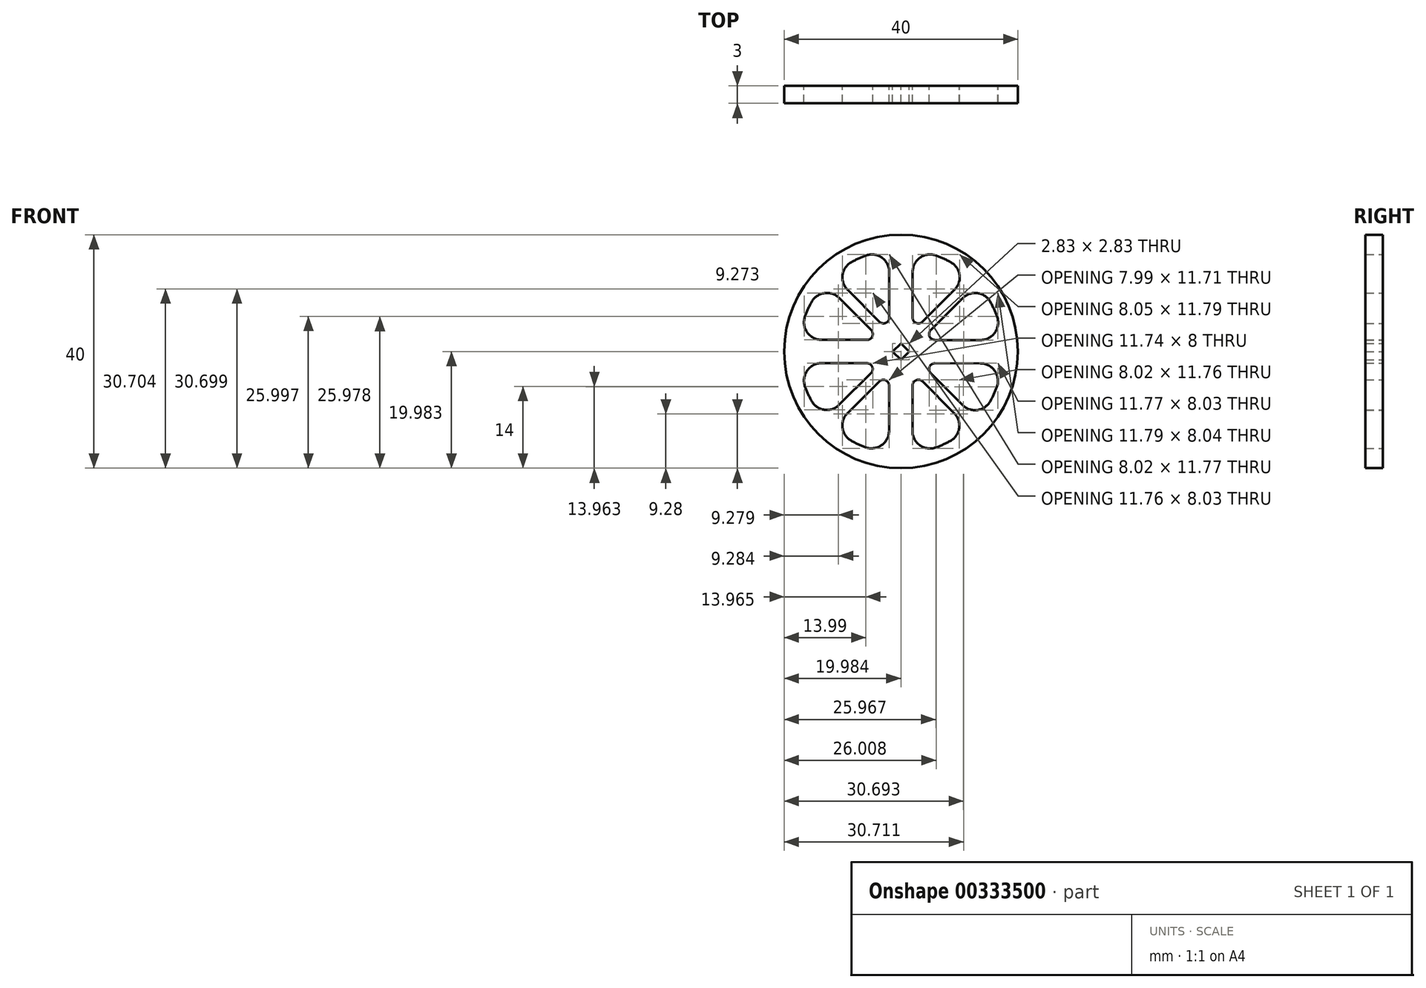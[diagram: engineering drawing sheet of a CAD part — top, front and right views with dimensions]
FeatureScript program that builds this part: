
annotation { "Feature Type Name" : "Feature", "Feature Type Description" : "" }
export const myFeature = defineFeature(function(context is Context, id is Id, definition is map)
    precondition{}
    {
        {
            var Q0;
            Q0=qCreatedBy(makeId("Front.planeOp"),FACE);
            var sketch = newSketch(context, id + "F0", { "sketchPlane" : qUnion([Q0])});
            skCircle(sketch, "E0", {"center": v(0, 0) * mm, "radius": 20 * mm});
            skArc(sketch, "E1", {"start": v(-16.43, -6.03) * mm, "mid": v(-15.92, -7.27) * mm, "end": v(-15.32, -8.46) * mm});
            skPoint(sketch, "E2", {"position": v(-2, 17.39) * mm});
            skPoint(sketch, "E3", {"position": v(2, 17.39) * mm});
            skPoint(sketch, "E4", {"position": v(-17.39, 2) * mm});
            skPoint(sketch, "E5", {"position": v(-17.39, -2) * mm});
            skPoint(sketch, "E6", {"position": v(-2.04, -17.38) * mm});
            skPoint(sketch, "E7", {"position": v(1.95, -17.4) * mm});
            skPoint(sketch, "E8", {"position": v(17.4, 1.95) * mm});
            skPoint(sketch, "E9", {"position": v(17.38, -2.05) * mm});
            skLineSegment(sketch, "E10", {"start": v(2, 13.62) * mm, "end": v(1.98, 5.8) * mm});
            skLineSegment(sketch, "E11", {"start": v(13.62, 1.96) * mm, "end": v(5.8, 1.97) * mm});
            skPoint(sketch, "E12.orphan", {"position": v(-17.5, 0) * mm});
            skLineSegment(sketch, "E13.trimOffspring", {"start": v(-2, 5.81) * mm, "end": v(-2, 13.6) * mm});
            skLineSegment(sketch, "E14.trimOffspring", {"start": v(1.97, -5.84) * mm, "end": v(1.96, -13.62) * mm});
            skLineSegment(sketch, "E15.trimOffspring", {"start": v(5.8, -2.02) * mm, "end": v(13.6, -2.04) * mm});
            skPoint(sketch, "E16.orphan", {"position": v(-0.04, -17.5) * mm});
            skArc(sketch, "E17.trimOffspring", {"start": v(5.98, -16.45) * mm, "mid": v(7.23, -15.94) * mm, "end": v(8.43, -15.33) * mm});
            skArc(sketch, "E18.trimOffspring", {"start": v(16.45, 5.98) * mm, "mid": v(15.93, 7.24) * mm, "end": v(15.32, 8.46) * mm});
            skPoint(sketch, "E19.orphan", {"position": v(17.5, -0.05) * mm});
            skLineSegment(sketch, "E20.trimOffspring", {"start": v(-5.84, 1.98) * mm, "end": v(-13.62, 2) * mm});
            skArc(sketch, "E21.trimOffspring", {"start": v(-6.04, 16.43) * mm, "mid": v(-7.28, 15.91) * mm, "end": v(-8.49, 15.3) * mm});
            skPoint(sketch, "E22.orphan", {"position": v(0, 17.5) * mm});
            skLineSegment(sketch, "E23", {"start": v(-13.6, -2) * mm, "end": v(-5.84, -2) * mm});
            skLineSegment(sketch, "E24", {"start": v(-2.04, -13.6) * mm, "end": v(-2.04, -5.86) * mm});
            skPoint(sketch, "E25", {"position": v(-13.06, 11.65) * mm});
            skPoint(sketch, "E26", {"position": v(-11.65, 13.06) * mm});
            skPoint(sketch, "E27", {"position": v(11.67, 13.05) * mm});
            skPoint(sketch, "E28", {"position": v(13.08, 11.63) * mm});
            skPoint(sketch, "E29", {"position": v(13.03, -11.68) * mm});
            skPoint(sketch, "E30", {"position": v(11.61, -13.1) * mm});
            skPoint(sketch, "E31", {"position": v(-11.66, -13.05) * mm});
            skPoint(sketch, "E32", {"position": v(-13.08, -11.63) * mm});
            skLineSegment(sketch, "E33", {"start": v(-10.56, 9.14) * mm, "end": v(-5.13, 3.7) * mm});
            skLineSegment(sketch, "E34", {"start": v(10.54, -9.18) * mm, "end": v(5.1, -3.73) * mm});
            skLineSegment(sketch, "E35", {"start": v(9.16, 10.55) * mm, "end": v(3.7, 5.1) * mm});
            skLineSegment(sketch, "E36", {"start": v(-9.16, -10.55) * mm, "end": v(-3.75, -5.15) * mm});
            skPoint(sketch, "E37.end.orphan", {"position": v(-12.37, 12.37) * mm});
            skLineSegment(sketch, "E38.trimOffspring", {"start": v(-3.71, 5.1) * mm, "end": v(-9.16, 10.56) * mm});
            skLineSegment(sketch, "E39.trimOffspring", {"start": v(-0.01, 1.4) * mm, "end": v(-1.43, -0.02) * mm});
            skLineSegment(sketch, "E40.trimOffspring", {"start": v(5.1, 3.68) * mm, "end": v(10.57, 9.13) * mm});
            skLineSegment(sketch, "E41.trimOffspring", {"start": v(1.4, -0.02) * mm, "end": v(-0.01, 1.4) * mm});
            skLineSegment(sketch, "E42.trimOffspring", {"start": v(3.68, -5.14) * mm, "end": v(9.11, -10.59) * mm});
            skPoint(sketch, "E43.end.orphan", {"position": v(12.34, -12.4) * mm});
            skLineSegment(sketch, "E44.trimOffspring", {"start": v(-5.14, -3.71) * mm, "end": v(-10.57, -9.14) * mm});
            skLineSegment(sketch, "E45.trimOffspring", {"start": v(-0.02, -1.43) * mm, "end": v(1.4, -0.02) * mm});
            skPoint(sketch, "E46.end.orphan", {"position": v(-12.39, -12.36) * mm});
            skPoint(sketch, "E47.end.orphan", {"position": v(12.4, 12.36) * mm});
            skLineSegment(sketch, "E48.trimOffspring", {"start": v(-1.43, -0.02) * mm, "end": v(-0.02, -1.43) * mm});
            skArc(sketch, "E49.trimOffspring", {"start": v(8.5, 15.3) * mm, "mid": v(7.29, 15.91) * mm, "end": v(6.03, 16.43) * mm});
            skArc(sketch, "E50.trimOffspring", {"start": v(-15.31, 8.48) * mm, "mid": v(-15.92, 7.27) * mm, "end": v(-16.43, 6.03) * mm});
            skArc(sketch, "E51.trimOffspring", {"start": v(-8.5, -15.3) * mm, "mid": v(-7.31, -15.9) * mm, "end": v(-6.08, -16.4) * mm});
            skArc(sketch, "E52.trimOffspring", {"start": v(15.28, -8.53) * mm, "mid": v(15.9, -7.33) * mm, "end": v(16.4, -6.08) * mm});
            skPoint(sketch, "E53.visualSharp", {"position": v(-3.43, -2) * mm});
            skArc(sketch, "E53.filletArc", {"start": v(-5.14, -3.71) * mm, "mid": v(-4.92, -2.62) * mm, "end": v(-5.84, -2) * mm});
            skPoint(sketch, "E54.visualSharp", {"position": v(1.97, -3.43) * mm});
            skArc(sketch, "E54.filletArc", {"start": v(3.68, -5.14) * mm, "mid": v(2.59, -4.92) * mm, "end": v(1.97, -5.84) * mm});
            skPoint(sketch, "E55.visualSharp", {"position": v(-2.04, -3.45) * mm});
            skArc(sketch, "E55.filletArc", {"start": v(-2.04, -5.86) * mm, "mid": v(-2.66, -4.93) * mm, "end": v(-3.75, -5.15) * mm});
            skPoint(sketch, "E56.visualSharp", {"position": v(3.39, -2.02) * mm});
            skArc(sketch, "E56.filletArc", {"start": v(5.8, -2.02) * mm, "mid": v(4.88, -2.64) * mm, "end": v(5.1, -3.73) * mm});
            skPoint(sketch, "E57.visualSharp", {"position": v(3.4, 1.97) * mm});
            skArc(sketch, "E57.filletArc", {"start": v(5.1, 3.68) * mm, "mid": v(4.88, 2.59) * mm, "end": v(5.8, 1.97) * mm});
            skPoint(sketch, "E58.visualSharp", {"position": v(1.98, 3.39) * mm});
            skArc(sketch, "E58.filletArc", {"start": v(1.98, 5.8) * mm, "mid": v(2.6, 4.88) * mm, "end": v(3.7, 5.1) * mm});
            skPoint(sketch, "E59.visualSharp", {"position": v(-2, 3.4) * mm});
            skArc(sketch, "E59.filletArc", {"start": v(-3.71, 5.1) * mm, "mid": v(-2.62, 4.89) * mm, "end": v(-2, 5.81) * mm});
            skPoint(sketch, "E60.visualSharp", {"position": v(-3.42, 1.98) * mm});
            skArc(sketch, "E60.filletArc", {"start": v(-5.84, 1.98) * mm, "mid": v(-4.91, 2.6) * mm, "end": v(-5.13, 3.7) * mm});
            skArc(sketch, "E61.filletArc", {"start": v(-16.43, 6.03) * mm, "mid": v(-16.07, 3.28) * mm, "end": v(-13.62, 2) * mm});
            skArc(sketch, "E62.filletArc", {"start": v(-10.56, 9.14) * mm, "mid": v(-13.1, 10) * mm, "end": v(-15.31, 8.48) * mm});
            skArc(sketch, "E63.filletArc", {"start": v(-8.49, 15.3) * mm, "mid": v(-10, 13.1) * mm, "end": v(-9.16, 10.56) * mm});
            skArc(sketch, "E64.filletArc", {"start": v(-2, 13.6) * mm, "mid": v(-3.28, 16.07) * mm, "end": v(-6.04, 16.43) * mm});
            skArc(sketch, "E65.filletArc", {"start": v(6.03, 16.43) * mm, "mid": v(3.28, 16.07) * mm, "end": v(2, 13.62) * mm});
            skArc(sketch, "E66.filletArc", {"start": v(15.32, 8.46) * mm, "mid": v(13.11, 9.98) * mm, "end": v(10.57, 9.13) * mm});
            skArc(sketch, "E67.filletArc", {"start": v(13.62, 1.96) * mm, "mid": v(16.08, 3.24) * mm, "end": v(16.45, 5.98) * mm});
            skArc(sketch, "E68.filletArc", {"start": v(16.4, -6.08) * mm, "mid": v(16.06, -3.33) * mm, "end": v(13.6, -2.04) * mm});
            skArc(sketch, "E69.filletArc", {"start": v(10.54, -9.18) * mm, "mid": v(13.07, -10.04) * mm, "end": v(15.28, -8.53) * mm});
            skArc(sketch, "E70.filletArc", {"start": v(8.43, -15.33) * mm, "mid": v(9.96, -13.13) * mm, "end": v(9.11, -10.59) * mm});
            skArc(sketch, "E71.filletArc", {"start": v(1.96, -13.62) * mm, "mid": v(3.24, -16.08) * mm, "end": v(5.98, -16.45) * mm});
            skArc(sketch, "E72.filletArc", {"start": v(-6.08, -16.4) * mm, "mid": v(-3.33, -16.06) * mm, "end": v(-2.04, -13.6) * mm});
            skArc(sketch, "E73.filletArc", {"start": v(-9.16, -10.55) * mm, "mid": v(-10.01, -13.09) * mm, "end": v(-8.5, -15.3) * mm});
            skArc(sketch, "E74.filletArc", {"start": v(-15.32, -8.46) * mm, "mid": v(-13.11, -9.98) * mm, "end": v(-10.57, -9.14) * mm});
            skArc(sketch, "E75.filletArc", {"start": v(-13.6, -2) * mm, "mid": v(-16.07, -3.28) * mm, "end": v(-16.43, -6.03) * mm});
            skArc(sketch, "E76.filletArc", {"start": v(9.16, 10.55) * mm, "mid": v(10.02, 13.09) * mm, "end": v(8.5, 15.3) * mm});
            skSolve(sketch);
        }
        {
            var Q0;
            Q0=makeQuery(id+"F0.imprint","IMPRINT",FACE,{"disambiguationData":[TD([[makeQuery(id+"F0.imprint","IMPRINT",EDGE,{"derivedFrom":sQuery(id+"F0.wireOp",EDGE,"E0")}),1.0]])]});
            extrude(context, id + "F1", {"entities" : qUnion([Q0]), "depth" : 3 * mm});
        }
    });
